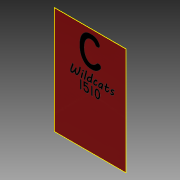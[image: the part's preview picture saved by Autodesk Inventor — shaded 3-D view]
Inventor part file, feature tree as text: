
AUTODESK INVENTOR PART (.ipt)
format: ipt  version: 2014 (Build 180170000, 170)  size: 83,456 bytes
history: native  units: in
note: dims shown in document units (in); Inventor stores cm internally (conversion verified against a paired STEP export)
features: sketch x2, extrude x1
ambient origin geometry x8: Origin, YZ Plane, XZ Plane, XY Plane, X Axis, Y Axis, Z Axis, Center Point
bodies: Solid1 (feature_tree)
feature tree (3):
  extrude  "Extrusion1"  Depth=36.0in
  sketch  "Sketch2"  dims[d2=0.01in d3=0.0in]
  sketch  "Sketch1"  dims[d0=24.0in d1=36.0in]
